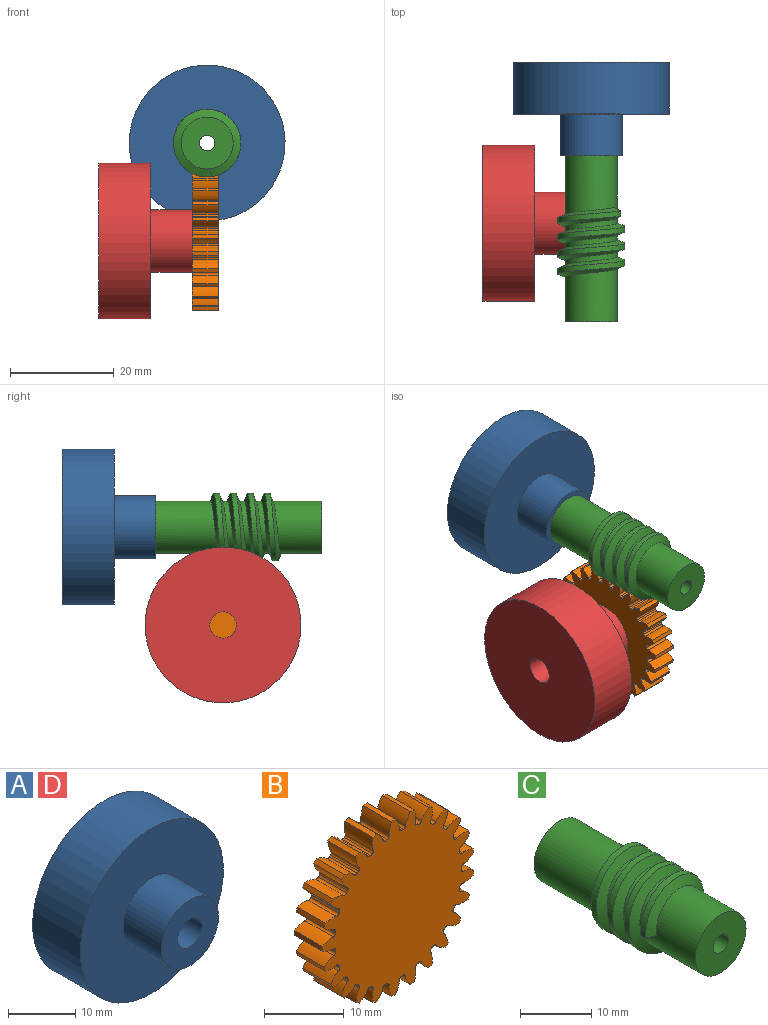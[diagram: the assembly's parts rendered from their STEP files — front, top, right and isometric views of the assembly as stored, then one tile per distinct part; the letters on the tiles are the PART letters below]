
ASSEMBLY  parts=4 mates=2
PART A: 6 faces, bbox 30x18x30 mm
  f0: cylinder r=2.55mm len=18mm, axis (0,1,0), area 288.4mm2, adj f3,f5
  f1: cylinder r=15mm len=30mm, axis (0,1,0), area 942.5mm2, adj f2,f3
  f2: plane 30x30mm, normal (0,-1,0), area 593.8mm2, adj f1,f4
  f3: plane 30x30mm, normal (0,1,0), area 686.4mm2, adj f0,f1
  f4: cylinder r=6mm len=12mm, axis (0,1,0), area 301.6mm2, adj f2,f5
  f5: plane 12x12mm, normal (0,-1,0), area 92.7mm2, adj f0,f4
PART B: 152 faces, bbox 26.9x5x27 mm
  f0: cylinder r=13.5mm len=5mm, axis (0,1,0), area 3.6mm2, adj f24,f26,f137,f149
  f1: cylinder r=13.5mm len=5mm, axis (0,1,0), area 3.6mm2, adj f24,f26,f144,f147
  f2: cylinder r=13.5mm len=5mm, axis (0,1,0), area 3.6mm2, adj f24,f26,f132,f139
  f3: cylinder r=13.5mm len=5mm, axis (0,1,0), area 3.6mm2, adj f24,f26,f127,f134
  f4: cylinder r=13.5mm len=5mm, axis (0,1,0), area 3.6mm2, adj f24,f26,f122,f129
  f5: cylinder r=13.5mm len=5mm, axis (0,1,0), area 3.6mm2, adj f24,f26,f112,f124
  f6: cylinder r=13.5mm len=5mm, axis (0,1,0), area 3.6mm2, adj f24,f26,f107,f119
  f7: cylinder r=13.5mm len=5mm, axis (0,1,0), area 3.6mm2, adj f24,f26,f114,f117
  f8: cylinder r=13.5mm len=5mm, axis (0,1,0), area 3.6mm2, adj f24,f26,f102,f109
  f9: cylinder r=13.5mm len=5mm, axis (0,1,0), area 3.6mm2, adj f24,f26,f97,f104
  f10: cylinder r=13.5mm len=5mm, axis (0,1,0), area 3.6mm2, adj f24,f26,f92,f99
  f11: cylinder r=13.5mm len=5mm, axis (0,1,0), area 3.6mm2, adj f24,f26,f77,f94
  f12: cylinder r=13.5mm len=5mm, axis (0,1,0), area 3.6mm2, adj f24,f26,f27,f89
  f13: cylinder r=13.5mm len=5mm, axis (0,1,0), area 3.6mm2, adj f24,f26,f84,f87
  f14: cylinder r=13.5mm len=5mm, axis (0,1,0), area 3.6mm2, adj f24,f26,f72,f79
  f15: cylinder r=13.5mm len=5mm, axis (0,1,0), area 3.6mm2, adj f24,f26,f74,f82
  f16: cylinder r=13.5mm len=5mm, axis (0,1,0), area 3.6mm2, adj f24,f26,f69,f142
  f17: cylinder r=13.5mm len=5mm, axis (0,1,0), area 3.6mm2, adj f24,f26,f64,f67
  f18: cylinder r=13.5mm len=5mm, axis (0,1,0), area 3.6mm2, adj f24,f26,f59,f62
  f19: cylinder r=13.5mm len=5mm, axis (0,1,0), area 3.6mm2, adj f24,f26,f54,f57
  f20: cylinder r=13.5mm len=5mm, axis (0,1,0), area 3.6mm2, adj f24,f26,f42,f49
  f21: cylinder r=13.5mm len=5mm, axis (0,1,0), area 3.6mm2, adj f24,f26,f32,f44
  f22: cylinder r=13.5mm len=5mm, axis (0,1,0), area 3.6mm2, adj f24,f26,f39,f52
  f23: cylinder r=13.5mm len=5mm, axis (0,1,0), area 3.6mm2, adj f24,f26,f34,f37
  f24: plane 26.99x26.94mm, normal (0,-1,0), area 483.6mm2, adj f0,f1,f2,f3,f4,f5,f6,f7
  f25: cylinder r=13.5mm len=5mm, axis (0,1,0), area 3.6mm2, adj f24,f26,f29,f47
  f26: plane 26.99x26.94mm, normal (0,1,0), area 483.6mm2, adj f0,f1,f2,f3,f4,f5,f6,f7
  f27: extruded ~5x1.82mm, area 10mm2, adj f12,f24,f26,f30
  f28: cylinder r=11.25mm len=5mm, axis (0,1,0), area 1.7mm2, adj f24,f26,f30,f31
  f29: extruded ~5x1.82mm, area 10mm2, adj f24,f25,f26,f31
  f30: cylinder r=0.38mm len=5mm, axis (0,1,0), area 2.9mm2, adj f24,f26,f27,f28
  f31: cylinder r=0.38mm len=5mm, axis (0,1,0), area 2.9mm2, adj f24,f26,f28,f29
  f32: extruded ~5x1.86mm, area 10mm2, adj f21,f24,f26,f35
  f33: cylinder r=11.25mm len=5mm, axis (0,1,0), area 1.7mm2, adj f24,f26,f35,f36
  f34: extruded ~5x1.82mm, area 10mm2, adj f23,f24,f26,f36
  f35: cylinder r=0.38mm len=5mm, axis (0,1,0), area 2.9mm2, adj f24,f26,f32,f33
  f36: cylinder r=0.38mm len=5mm, axis (0,1,0), area 2.9mm2, adj f24,f26,f33,f34
  f37: extruded ~5x1.63mm, area 10mm2, adj f23,f24,f26,f40
  f38: cylinder r=11.25mm len=5mm, axis (0,1,0), area 1.7mm2, adj f24,f26,f40,f41
  f39: extruded ~5x1.96mm, area 10mm2, adj f22,f24,f26,f41
  f40: cylinder r=0.38mm len=5mm, axis (0,1,0), area 2.9mm2, adj f24,f26,f37,f38
  f41: cylinder r=0.38mm len=5mm, axis (0,1,0), area 2.9mm2, adj f24,f26,f38,f39
  f42: extruded ~5x1.97mm, area 10mm2, adj f20,f24,f26,f45
  f43: cylinder r=11.25mm len=5mm, axis (0,1,0), area 1.7mm2, adj f24,f26,f45,f46
  f44: extruded ~5x1.56mm, area 10mm2, adj f21,f24,f26,f46
  f45: cylinder r=0.38mm len=5mm, axis (0,1,0), area 2.9mm2, adj f24,f26,f42,f43
  f46: cylinder r=0.38mm len=5mm, axis (0,1,0), area 2.9mm2, adj f24,f26,f43,f44
  f47: extruded ~5x1.96mm, area 10mm2, adj f24,f25,f26,f50
  f48: cylinder r=11.25mm len=5mm, axis (0,1,0), area 1.7mm2, adj f24,f26,f50,f51
  f49: extruded ~5x1.57mm, area 10mm2, adj f20,f24,f26,f51
  f50: cylinder r=0.38mm len=5mm, axis (0,1,0), area 2.9mm2, adj f24,f26,f47,f48
  f51: cylinder r=0.38mm len=5mm, axis (0,1,0), area 2.9mm2, adj f24,f26,f48,f49
  f52: extruded ~5x1.5mm, area 10mm2, adj f22,f24,f26,f55
  f53: cylinder r=11.25mm len=5mm, axis (0,1,0), area 1.7mm2, adj f24,f26,f55,f56
  f54: extruded ~5x1.98mm, area 10mm2, adj f19,f24,f26,f56
  f55: cylinder r=0.38mm len=5mm, axis (0,1,0), area 2.9mm2, adj f24,f26,f52,f53
  f56: cylinder r=0.38mm len=5mm, axis (0,1,0), area 2.9mm2, adj f24,f26,f53,f54
  f57: extruded ~5x1.77mm, area 10mm2, adj f19,f24,f26,f60
  f58: cylinder r=11.25mm len=5mm, axis (0,1,0), area 1.7mm2, adj f24,f26,f60,f61
  f59: extruded ~5x1.87mm, area 10mm2, adj f18,f24,f26,f61
  f60: cylinder r=0.38mm len=5mm, axis (0,1,0), area 2.9mm2, adj f24,f26,f57,f58
  f61: cylinder r=0.38mm len=5mm, axis (0,1,0), area 2.9mm2, adj f24,f26,f58,f59
  f62: extruded ~5x1.94mm, area 10mm2, adj f18,f24,f26,f65
  f63: cylinder r=11.25mm len=5mm, axis (0,1,0), area 1.7mm2, adj f24,f26,f65,f66
  f64: extruded ~5x1.65mm, area 10mm2, adj f17,f24,f26,f66
  f65: cylinder r=0.38mm len=5mm, axis (0,1,0), area 2.9mm2, adj f24,f26,f62,f63
  f66: cylinder r=0.38mm len=5mm, axis (0,1,0), area 2.9mm2, adj f24,f26,f63,f64
  f67: extruded ~5x1.98mm, area 10mm2, adj f17,f24,f26,f70
  f68: cylinder r=11.25mm len=5mm, axis (0,1,0), area 1.7mm2, adj f24,f26,f70,f71
  f69: extruded ~5x1.48mm, area 10mm2, adj f16,f24,f26,f71
  f70: cylinder r=0.38mm len=5mm, axis (0,1,0), area 2.9mm2, adj f24,f26,f67,f68
  f71: cylinder r=0.38mm len=5mm, axis (0,1,0), area 2.9mm2, adj f24,f26,f68,f69
  f72: extruded ~5x1.82mm, area 10mm2, adj f14,f24,f26,f75
  f73: cylinder r=11.25mm len=5mm, axis (0,1,0), area 1.7mm2, adj f24,f26,f75,f76
  f74: extruded ~5x1.86mm, area 10mm2, adj f15,f24,f26,f76
  f75: cylinder r=0.38mm len=5mm, axis (0,1,0), area 2.9mm2, adj f24,f26,f72,f73
  f76: cylinder r=0.38mm len=5mm, axis (0,1,0), area 2.9mm2, adj f24,f26,f73,f74
  f77: extruded ~5x1.96mm, area 10mm2, adj f11,f24,f26,f80
  f78: cylinder r=11.25mm len=5mm, axis (0,1,0), area 1.7mm2, adj f24,f26,f80,f81
  f79: extruded ~5x1.63mm, area 10mm2, adj f14,f24,f26,f81
  f80: cylinder r=0.38mm len=5mm, axis (0,1,0), area 2.9mm2, adj f24,f26,f77,f78
  f81: cylinder r=0.38mm len=5mm, axis (0,1,0), area 2.9mm2, adj f24,f26,f78,f79
  f82: extruded ~5x1.56mm, area 10mm2, adj f15,f24,f26,f85
  f83: cylinder r=11.25mm len=5mm, axis (0,1,0), area 1.7mm2, adj f24,f26,f85,f86
  f84: extruded ~5x1.97mm, area 10mm2, adj f13,f24,f26,f86
  f85: cylinder r=0.38mm len=5mm, axis (0,1,0), area 2.9mm2, adj f24,f26,f82,f83
  f86: cylinder r=0.38mm len=5mm, axis (0,1,0), area 2.9mm2, adj f24,f26,f83,f84
  f87: extruded ~5x1.57mm, area 10mm2, adj f13,f24,f26,f90
  f88: cylinder r=11.25mm len=5mm, axis (0,1,0), area 1.7mm2, adj f24,f26,f90,f91
  f89: extruded ~5x1.96mm, area 10mm2, adj f12,f24,f26,f91
  f90: cylinder r=0.38mm len=5mm, axis (0,1,0), area 2.9mm2, adj f24,f26,f87,f88
  f91: cylinder r=0.38mm len=5mm, axis (0,1,0), area 2.9mm2, adj f24,f26,f88,f89
  f92: extruded ~5x1.98mm, area 10mm2, adj f10,f24,f26,f95
  f93: cylinder r=11.25mm len=5mm, axis (0,1,0), area 1.7mm2, adj f24,f26,f95,f96
  f94: extruded ~5x1.5mm, area 10mm2, adj f11,f24,f26,f96
  f95: cylinder r=0.38mm len=5mm, axis (0,1,0), area 2.9mm2, adj f24,f26,f92,f93
  f96: cylinder r=0.38mm len=5mm, axis (0,1,0), area 2.9mm2, adj f24,f26,f93,f94
  f97: extruded ~5x1.87mm, area 10mm2, adj f9,f24,f26,f100
  f98: cylinder r=11.25mm len=5mm, axis (0,1,0), area 1.7mm2, adj f24,f26,f100,f101
  f99: extruded ~5x1.77mm, area 10mm2, adj f10,f24,f26,f101
  f100: cylinder r=0.38mm len=5mm, axis (0,1,0), area 2.9mm2, adj f24,f26,f97,f98
  f101: cylinder r=0.38mm len=5mm, axis (0,1,0), area 2.9mm2, adj f24,f26,f98,f99
  f102: extruded ~5x1.65mm, area 10mm2, adj f8,f24,f26,f105
  f103: cylinder r=11.25mm len=5mm, axis (0,1,0), area 1.7mm2, adj f24,f26,f105,f106
  f104: extruded ~5x1.94mm, area 10mm2, adj f9,f24,f26,f106
  f105: cylinder r=0.38mm len=5mm, axis (0,1,0), area 2.9mm2, adj f24,f26,f102,f103
  f106: cylinder r=0.38mm len=5mm, axis (0,1,0), area 2.9mm2, adj f24,f26,f103,f104
  f107: extruded ~5x1.48mm, area 10mm2, adj f6,f24,f26,f110
  f108: cylinder r=11.25mm len=5mm, axis (0,1,0), area 1.7mm2, adj f24,f26,f110,f111
  f109: extruded ~5x1.98mm, area 10mm2, adj f8,f24,f26,f111
  f110: cylinder r=0.38mm len=5mm, axis (0,1,0), area 2.9mm2, adj f24,f26,f107,f108
  f111: cylinder r=0.38mm len=5mm, axis (0,1,0), area 2.9mm2, adj f24,f26,f108,f109
  f112: extruded ~5x1.93mm, area 10mm2, adj f5,f24,f26,f115
  f113: cylinder r=11.25mm len=5mm, axis (0,1,0), area 1.7mm2, adj f24,f26,f115,f116
  f114: extruded ~5x1.7mm, area 10mm2, adj f7,f24,f26,f116
  f115: cylinder r=0.38mm len=5mm, axis (0,1,0), area 2.9mm2, adj f24,f26,f112,f113
  f116: cylinder r=0.38mm len=5mm, axis (0,1,0), area 2.9mm2, adj f24,f26,f113,f114
  f117: extruded ~5x1.76mm, area 10mm2, adj f7,f24,f26,f120
  f118: cylinder r=11.25mm len=5mm, axis (0,1,0), area 1.7mm2, adj f24,f26,f120,f121
  f119: extruded ~5x1.9mm, area 10mm2, adj f6,f24,f26,f121
  f120: cylinder r=0.38mm len=5mm, axis (0,1,0), area 2.9mm2, adj f24,f26,f117,f118
  f121: cylinder r=0.38mm len=5mm, axis (0,1,0), area 2.9mm2, adj f24,f26,f118,f119
  f122: extruded ~5x1.98mm, area 10mm2, adj f4,f24,f26,f125
  f123: cylinder r=11.25mm len=5mm, axis (0,1,0), area 1.7mm2, adj f24,f26,f125,f126
  f124: extruded ~5x1.41mm, area 10mm2, adj f5,f24,f26,f126
  f125: cylinder r=0.38mm len=5mm, axis (0,1,0), area 2.9mm2, adj f24,f26,f122,f123
  f126: cylinder r=0.38mm len=5mm, axis (0,1,0), area 2.9mm2, adj f24,f26,f123,f124
  f127: extruded ~5x1.91mm, area 10mm2, adj f3,f24,f26,f130
  f128: cylinder r=11.25mm len=5mm, axis (0,1,0), area 1.7mm2, adj f24,f26,f130,f131
  f129: extruded ~5x1.71mm, area 10mm2, adj f4,f24,f26,f131
  f130: cylinder r=0.38mm len=5mm, axis (0,1,0), area 2.9mm2, adj f24,f26,f127,f128
  f131: cylinder r=0.38mm len=5mm, axis (0,1,0), area 2.9mm2, adj f24,f26,f128,f129
  f132: extruded ~5x1.71mm, area 10mm2, adj f2,f24,f26,f135
  f133: cylinder r=11.25mm len=5mm, axis (0,1,0), area 1.7mm2, adj f24,f26,f135,f136
  f134: extruded ~5x1.91mm, area 10mm2, adj f3,f24,f26,f136
  f135: cylinder r=0.38mm len=5mm, axis (0,1,0), area 2.9mm2, adj f24,f26,f132,f133
  f136: cylinder r=0.38mm len=5mm, axis (0,1,0), area 2.9mm2, adj f24,f26,f133,f134
  f137: extruded ~5x1.41mm, area 10mm2, adj f0,f24,f26,f140
  f138: cylinder r=11.25mm len=5mm, axis (0,1,0), area 1.7mm2, adj f24,f26,f140,f141
  f139: extruded ~5x1.98mm, area 10mm2, adj f2,f24,f26,f141
  f140: cylinder r=0.38mm len=5mm, axis (0,1,0), area 2.9mm2, adj f24,f26,f137,f138
  f141: cylinder r=0.38mm len=5mm, axis (0,1,0), area 2.9mm2, adj f24,f26,f138,f139
  f142: extruded ~5x1.9mm, area 10mm2, adj f16,f24,f26,f145
  f143: cylinder r=11.25mm len=5mm, axis (0,1,0), area 1.7mm2, adj f24,f26,f145,f146
  f144: extruded ~5x1.76mm, area 10mm2, adj f1,f24,f26,f146
  f145: cylinder r=0.38mm len=5mm, axis (0,1,0), area 2.9mm2, adj f24,f26,f142,f143
  f146: cylinder r=0.38mm len=5mm, axis (0,1,0), area 2.9mm2, adj f24,f26,f143,f144
  f147: extruded ~5x1.7mm, area 10mm2, adj f1,f24,f26,f150
  f148: cylinder r=11.25mm len=5mm, axis (0,1,0), area 1.7mm2, adj f24,f26,f150,f151
  f149: extruded ~5x1.93mm, area 10mm2, adj f0,f24,f26,f151
  f150: cylinder r=0.38mm len=5mm, axis (0,1,0), area 2.9mm2, adj f24,f26,f147,f148
  f151: cylinder r=0.38mm len=5mm, axis (0,1,0), area 2.9mm2, adj f24,f26,f148,f149
PART C: 11 faces, bbox 13x32x15 mm
  f0: cylinder r=1.5mm len=32mm, axis (0,1,0), area 301.6mm2, adj f9,f10
  f1: cylinder r=5mm len=16.31mm, axis (0,1,0), area 394.8mm2, adj f2,f5,f6,f8,f9
  f2: cylinder r=5mm len=10mm, axis (0,1,0), area 31.4mm2, adj f1,f3,f6,f8
  f3: cylinder r=5mm len=13.44mm, axis (0,1,0), area 318.1mm2, adj f2,f4,f6,f8,f10
  f4: plane 2.25x1.5mm, normal (0,0,-1), area 2.4mm2, adj f3,f6,f7,f8
  f5: plane 2.26x1.41mm, normal (-0.94,0,-0.35), area 2.4mm2, adj f1,f6,f7,f8
  f6: bspline ~15.01x13.08mm, area 217.5mm2, adj f1,f2,f3,f4,f5,f7
  f7: cylinder r=6.5mm len=13mm, axis (0,1,0), area 150.4mm2, adj f4,f5,f6,f8
  f8: bspline ~15.01x13.08mm, area 217.5mm2, adj f1,f2,f3,f4,f5,f7
  f9: plane 10x10mm, normal (0,1,0), area 71.5mm2, adj f0,f1
  f10: plane 10x10mm, normal (0,-1,0), area 71.5mm2, adj f0,f3
PART D: same geometry as A
PLACE A t=(0,18,0)mm fixed
PLACE B rot(axis=(0.52,0.52,-0.68),111.9deg) t=(2.16,-12.98,-18.85)mm
PLACE C rot(axis=(0,-1,0),97.3deg) t=(0,-10,0)mm
PLACE D rot(axis=(0.71,-0.71,0),180deg) t=(-20.84,-12.98,-18.85)mm fixed
MATE revolute D.f4 <-> B.f0  axis (1,0,0) through (-2.84,-12.98,-18.85)mm
MATE revolute A.f4 <-> C.f1  axis (0,1,0) through (0,0,0)mm
